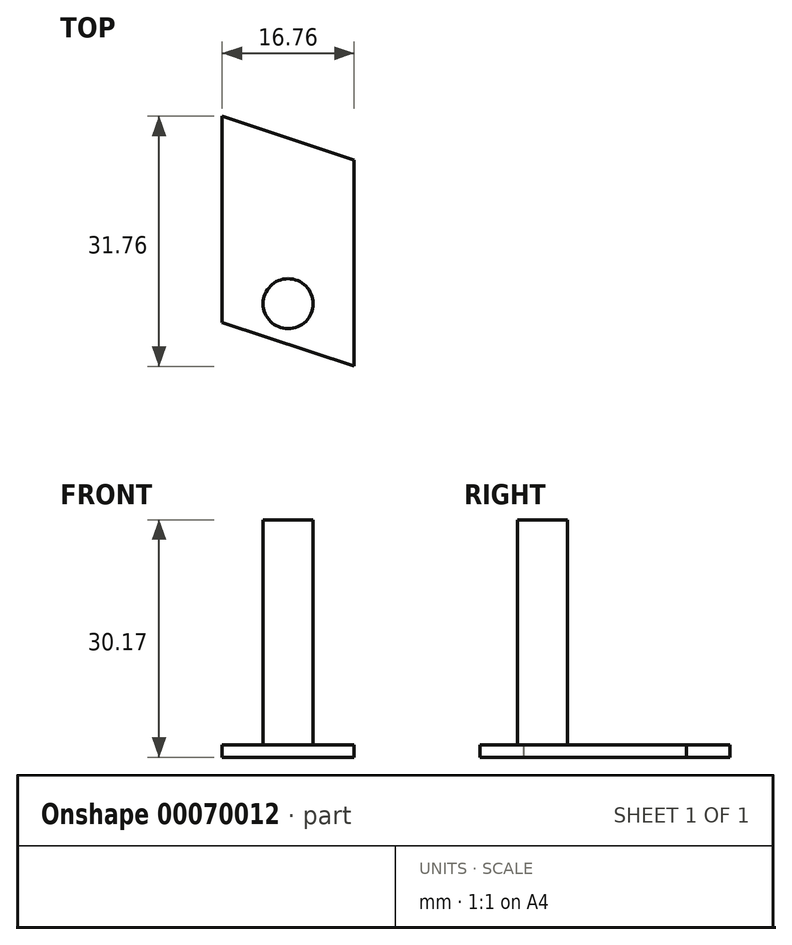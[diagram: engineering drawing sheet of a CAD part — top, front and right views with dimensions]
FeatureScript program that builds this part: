
annotation { "Feature Type Name" : "Feature", "Feature Type Description" : "" }
export const myFeature = defineFeature(function(context is Context, id is Id, definition is map)
    precondition{}
    {
        {
            var Q0;
            Q0=qCreatedBy(makeId("Top.planeOp"),FACE);
            var sketch = newSketch(context, id + "F0", { "sketchPlane" : qUnion([Q0])});
            skLineSegment(sketch, "E0.bottom", {"start": v(-8.38, 15.88) * mm, "end": v(8.38, 15.88) * mm, "construction": true});
            skLineSegment(sketch, "E0.top", {"start": v(-8.38, -15.88) * mm, "end": v(8.38, -15.88) * mm, "construction": true});
            skLineSegment(sketch, "E0.left", {"start": v(-8.38, 15.88) * mm, "end": v(-8.38, -15.88) * mm, "construction": true});
            skLineSegment(sketch, "E0.right", {"start": v(8.38, 15.88) * mm, "end": v(8.38, -15.88) * mm, "construction": true});
            skPoint(sketch, "E0.middle", {"position": v(0, 0) * mm});
            skLineSegment(sketch, "E1", {"start": v(8.38, 15.88) * mm, "end": v(-8.38, 10.32) * mm, "construction": true});
            skLineSegment(sketch, "E2", {"start": v(-8.38, -15.88) * mm, "end": v(8.38, -10.32) * mm, "construction": true});
            skLineSegment(sketch, "E3", {"start": v(-8.38, 10.32) * mm, "end": v(-8.38, -15.88) * mm, "construction": true});
            skLineSegment(sketch, "E4", {"start": v(8.38, -10.32) * mm, "end": v(8.38, 15.88) * mm, "construction": true});
            skCircle(sketch, "E5", {"center": v(0, -7.94) * mm, "radius": 7.24 * mm, "construction": true});
            skCircle(sketch, "E6", {"center": v(0, -7.94) * mm, "radius": 3.18 * mm, "construction": true});
            skLineSegment(sketch, "E7", {"start": v(-8.38, 0) * mm, "end": v(8.38, 0) * mm, "construction": true});
            skLineSegment(sketch, "E8", {"start": v(0, 0) * mm, "end": v(0, -15.88) * mm, "construction": true});
            skLineSegment(sketch, "E9", {"start": v(8.38, -15.88) * mm, "end": v(-8.38, -10.32) * mm});
            skLineSegment(sketch, "E10", {"start": v(-8.38, -10.32) * mm, "end": v(-8.38, 15.88) * mm});
            skLineSegment(sketch, "E11", {"start": v(8.38, 10.32) * mm, "end": v(-8.38, 15.88) * mm});
            skLineSegment(sketch, "E12", {"start": v(8.38, 10.32) * mm, "end": v(8.38, -15.88) * mm});
            skSolve(sketch);
        }
        {
            var Q0;
            Q0=qSketchRegion(id+"F0",true);
            extrude(context, id + "F1", {"entities" : qUnion([Q0]), "oppositeDirection" : true, "depth" : 1.59 * mm});
        }
        {
            var Q0;
            Q0=qCreatedBy(makeId("Top.planeOp"),FACE);
            var sketch = newSketch(context, id + "F2", { "sketchPlane" : qUnion([Q0])});
            skCircle(sketch, "E13.0", {"center": v(0, -7.94) * mm, "radius": 3.18 * mm});
            skSolve(sketch);
        }
        {
            var Q0;
            Q0=qSketchRegion(id+"F2",true);
            extrude(context, id + "F3", {"entities" : qUnion([Q0]), "operationType" : NewBodyOperationType.ADD, "depth" : 28.57 * mm});
        }
    });
